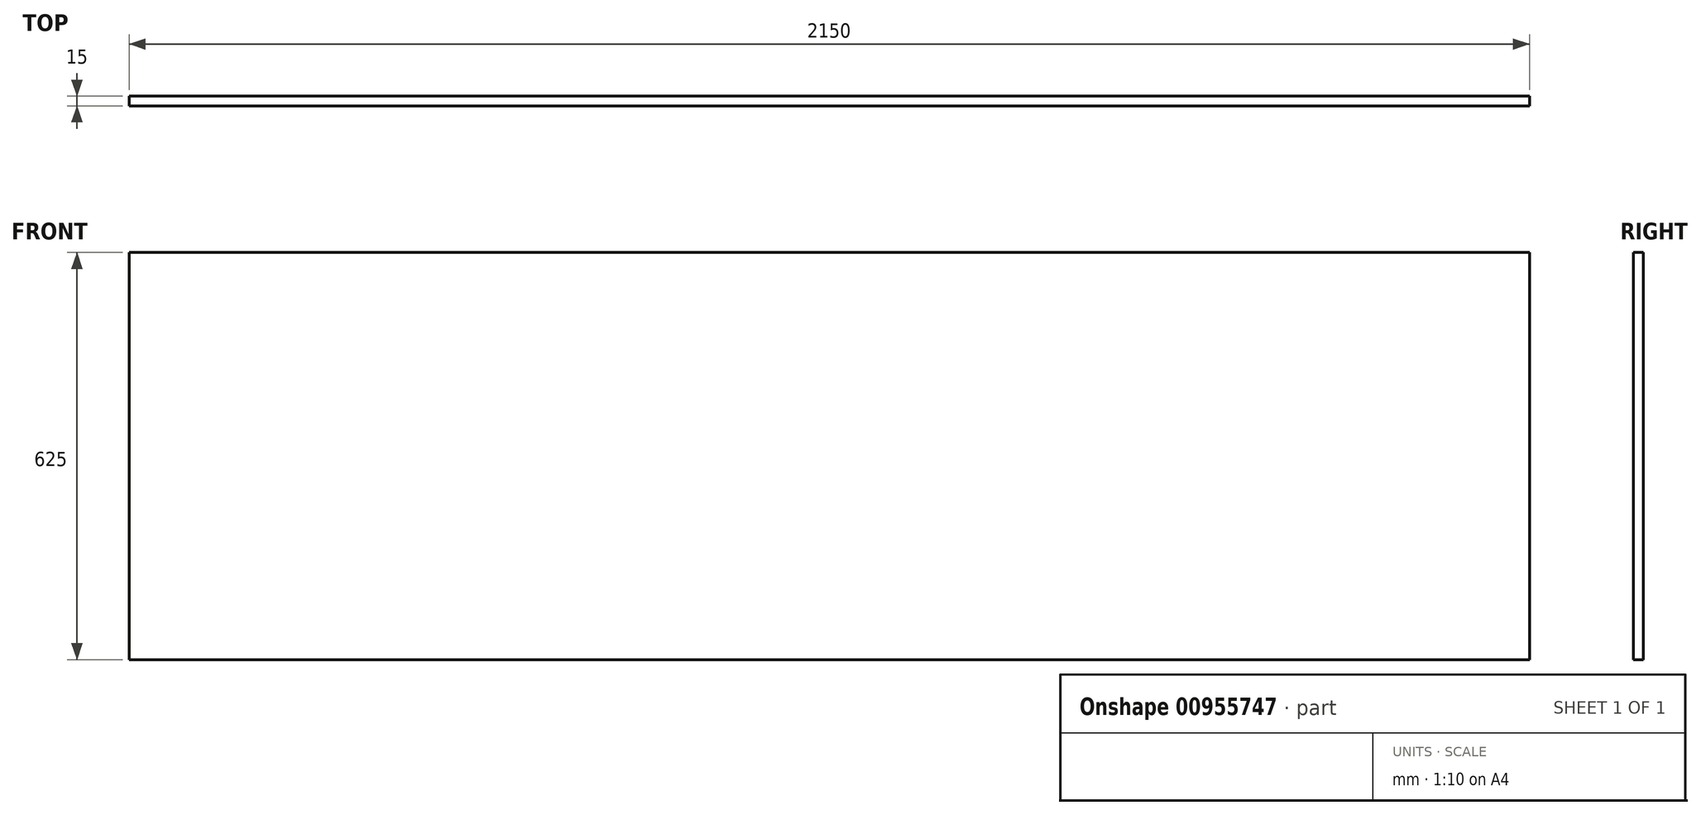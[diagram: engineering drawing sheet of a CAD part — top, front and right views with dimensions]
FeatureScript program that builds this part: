
annotation { "Feature Type Name" : "Feature", "Feature Type Description" : "" }
export const myFeature = defineFeature(function(context is Context, id is Id, definition is map)
    precondition{}
    {
        {
            var Q0;
            Q0=qCreatedBy(makeId("Front.planeOp"),FACE);
            var sketch = newSketch(context, id + "F0", { "sketchPlane" : qUnion([Q0])});
            skLineSegment(sketch, "E0", {"start": v(0, 0) * mm, "end": v(0, -625) * mm});
            skLineSegment(sketch, "E1", {"start": v(0, -625) * mm, "end": v(2150, -625) * mm});
            skLineSegment(sketch, "E2", {"start": v(0, 0) * mm, "end": v(2150, 0) * mm});
            skLineSegment(sketch, "E3", {"start": v(2150, -625) * mm, "end": v(2150, 0) * mm});
            skSolve(sketch);
        }
        {
            var Q0;
            Q0 = qSketchRegion(id + "F0", true);
            extrude(context, id + "F1", {"entities" : qUnion([Q0]), "depth" : 15 * mm, "offsetDistance" : 25 * mm});
        }
    });
